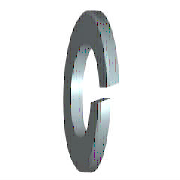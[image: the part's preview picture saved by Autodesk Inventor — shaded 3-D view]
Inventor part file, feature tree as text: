
AUTODESK INVENTOR PART (.ipt)
format: ipt  version: 2024 (Build 280153000, 153)  size: 125,952 bytes
history: native  units: mm (DEFAULTED — no unit token found)
features: sketch x2, extrude x1, other x1, plane x1
ambient origin geometry x6: Origin, YZ Plane, X Axis, Y Axis, Z Axis, Center Point
bodies: Solid1 (feature_tree), Body (feature_tree)
feature tree (5):
  extrude  "Cut"  Depth=7.55mm
  other  "Work Axis1"
  plane  "Work Plane1"
  sketch  "Sketch1"  dims[d0=4.1mm d1=7.55mm]
  sketch  "Sketch2"  dims[d2=0.9mm d3=0.0mm d4=0.18mm d5=0.18mm d6=12.217305mm d7=0.9mm d8=0.0mm d9=0.0mm d10=0.0mm d11=0.0mm d12=0.0mm]
